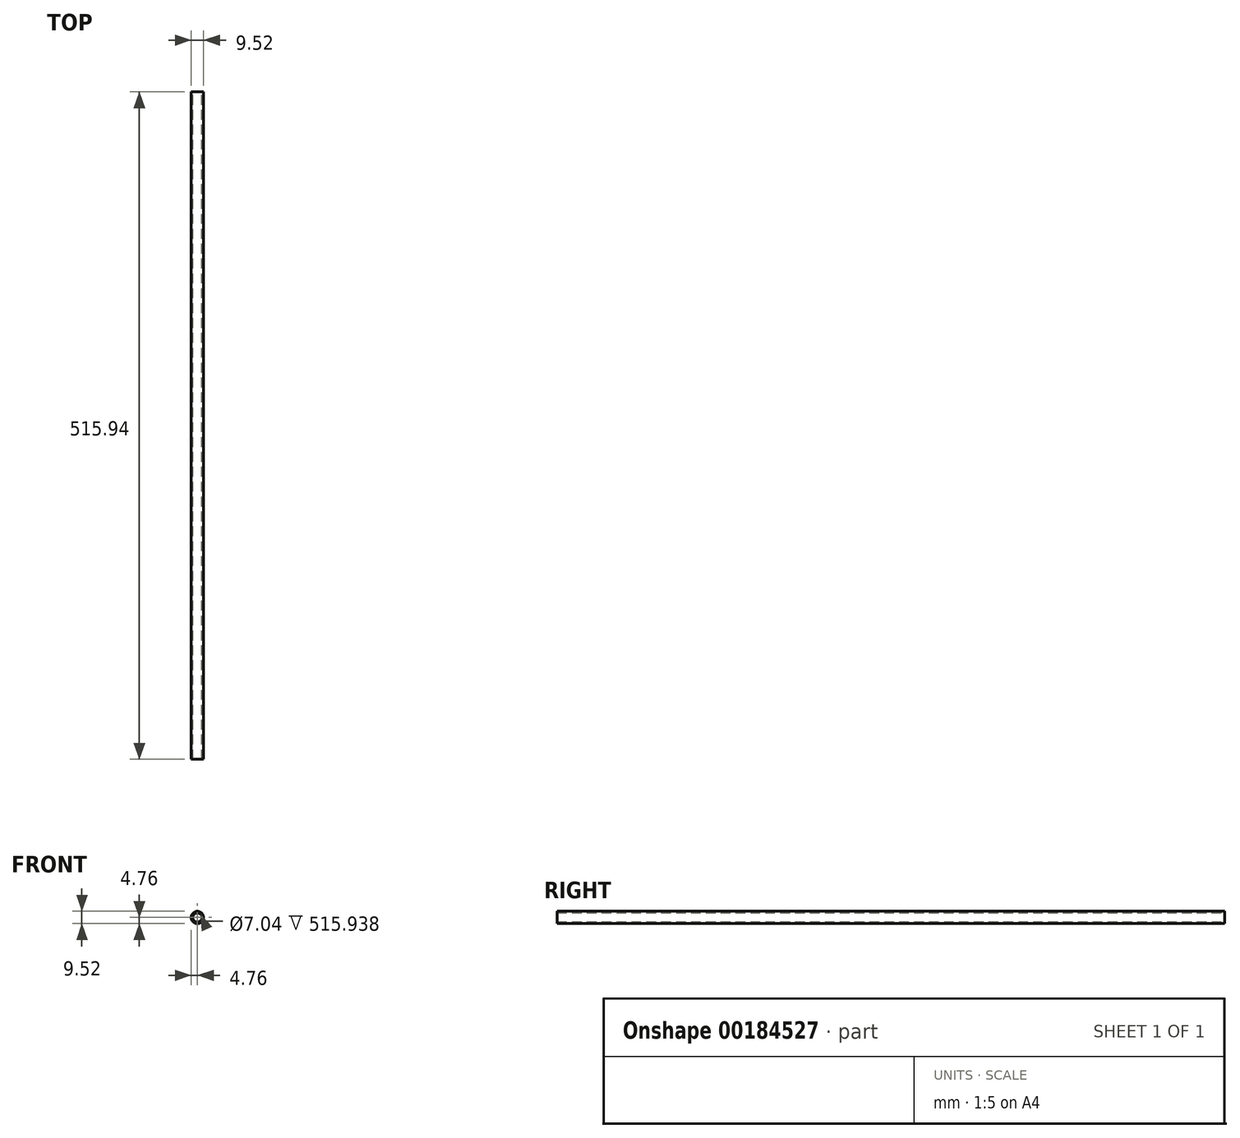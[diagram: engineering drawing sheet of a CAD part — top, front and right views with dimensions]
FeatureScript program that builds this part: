
annotation { "Feature Type Name" : "Feature", "Feature Type Description" : "" }
export const myFeature = defineFeature(function(context is Context, id is Id, definition is map)
    precondition{}
    {
        {
            var Q0;
            Q0=qCreatedBy(makeId("Front.planeOp"),FACE);
            var sketch = newSketch(context, id + "F0", { "sketchPlane" : qUnion([Q0])});
            skCircle(sketch, "E0", {"center": v(0, 0) * mm, "radius": 4.76 * mm});
            skCircle(sketch, "E1.0", {"center": v(0, 0) * mm, "radius": 3.52 * mm});
            skSolve(sketch);
        }
        {
            var Q0;
            Q0=makeQuery(id+"F0.imprint","IMPRINT",FACE,{"disambiguationData":[TD([[makeQuery(id+"F0.imprint","IMPRINT",EDGE,{"derivedFrom":sQuery(id+"F0.wireOp",EDGE,"E0")}),1.0]])]});
            extrude(context, id + "F1", {"entities" : qUnion([Q0]), "endBound" : BoundingType.SYMMETRIC, "depth" : 515.94 * mm});
        }
    });
